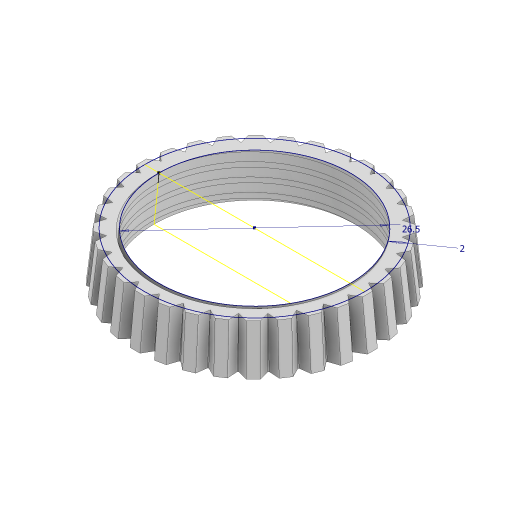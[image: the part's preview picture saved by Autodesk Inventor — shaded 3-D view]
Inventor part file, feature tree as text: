
AUTODESK INVENTOR PART (.ipt)
format: ipt  version: 2023 (Build 270158000, 158)  size: 495,104 bytes
history: native  units: mm
features: sketch x5, draft x2, helix x2, projected_geometry x2, extrude x1, sweep x1, pattern_circular x1
ambient origin geometry x8: Origin, YZ Plane, XZ Plane, XY Plane, X Axis, Y Axis, Z Axis, Center Point
bodies: Solid1 (feature_tree)
feature tree (14):
  extrude  "Extrusion1"  Depth=6.52mm TaperAngle=0.0deg
  draft  "FaceDraft1"
  sketch  "Sketch2"  dims[d7=2.0mm d8=9.0mm d9=10.0mm d10=1.047198mm d11=90.0deg d12=90.0deg d13=0.0mm d14=0.0mm d15=2.0mm d16=3.0mm d17=10.0mm d18=-1.047198mm d19=90.0deg d20=90.0deg d21=0.0mm d22=0.0mm d23=2.0mm d99=1.2mm]
  sketch  "Sketch4"  dims[d100=30.0deg d101=30.0deg]
  helix  "Coil1"  [1 undecoded]
  helix  "Coil2"  [1 undecoded]
  draft  "FaceDraft2"
  sweep  "Sweep1"
  pattern_circular  "Circular Pattern4"  [2 undecoded]
  sketch  "Sketch1"  dims[d0=26.5mm d2=6.52mm d3=0.0mm d4=1.047198mm]
  sketch  "Sketch9"  dims[d104=1.047198mm]
  sketch  "Sketch11"  dims[d105=14.5645mm d106=0.0mm d107=0.0mm d108=320.0mm d109=360.0deg]
  projected_geometry  "Project Cut Edges1"
  projected_geometry  "Project Cut Edges2"
note: 4 required parameter values undecoded (feature->parameter linkage not recoverable at this tier; creation-order binding heuristic only, values carry confidence <= 0.55)
